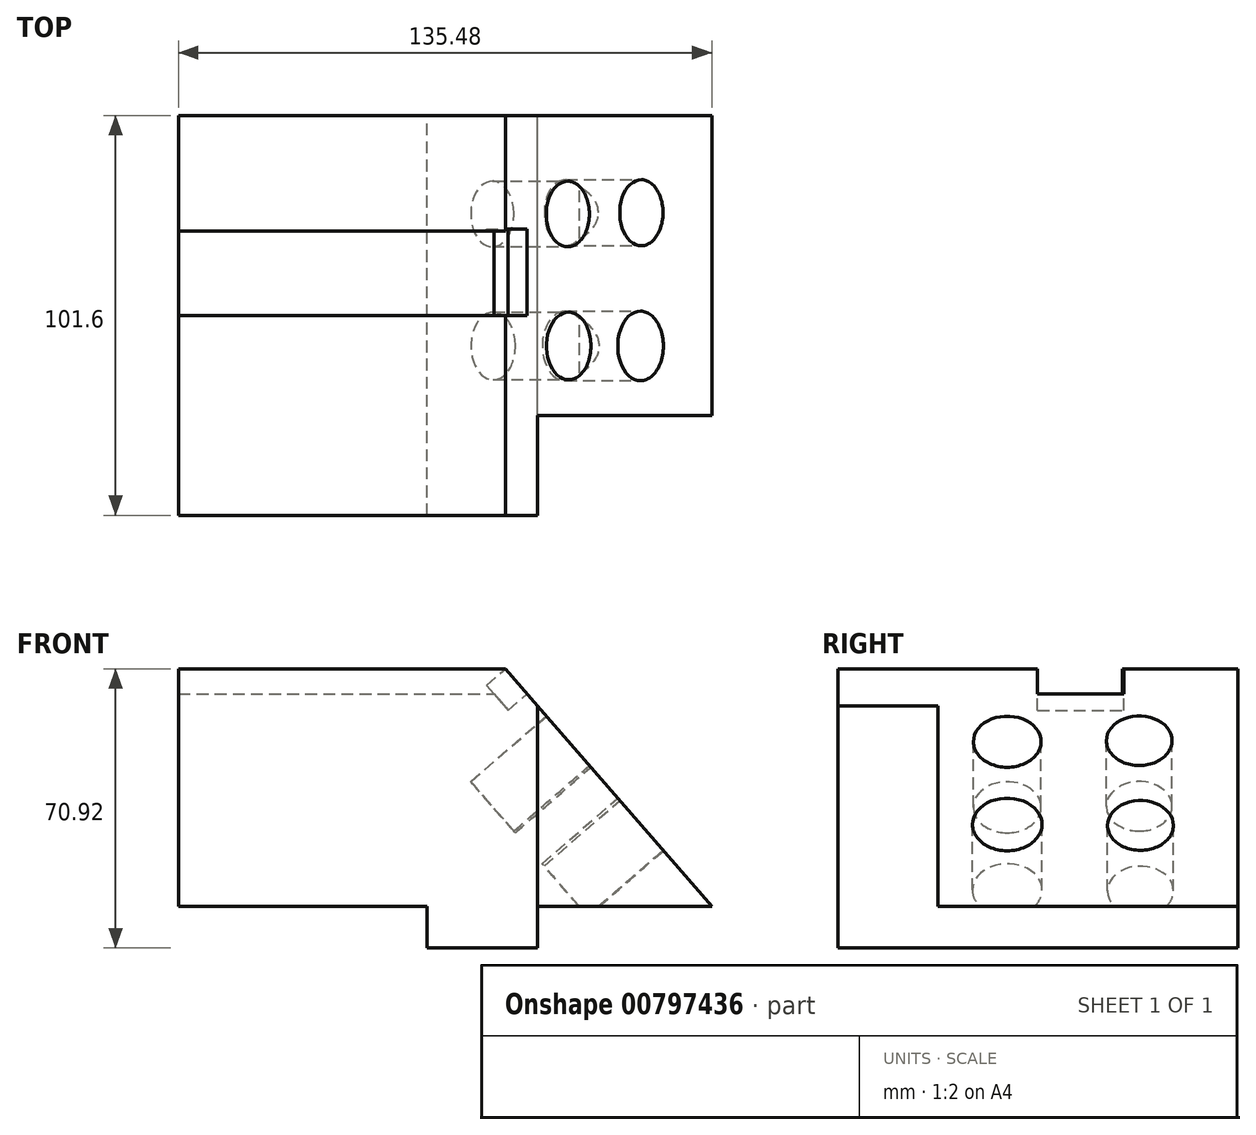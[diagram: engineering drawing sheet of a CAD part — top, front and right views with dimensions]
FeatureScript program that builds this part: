
annotation { "Feature Type Name" : "Feature", "Feature Type Description" : "" }
export const myFeature = defineFeature(function(context is Context, id is Id, definition is map)
    precondition{}
    {
        {
            var Q0;
            Q0=qCreatedBy(makeId("Front.planeOp"),FACE);
            var sketch = newSketch(context, id + "F0", { "sketchPlane" : qUnion([Q0])});
            skLineSegment(sketch, "E0.bottom", {"start": v(-53.31, 36.98) * mm, "end": v(29.7, 36.98) * mm});
            skLineSegment(sketch, "E0.top", {"start": v(-53.31, -23.38) * mm, "end": v(9.77, -23.38) * mm});
            skLineSegment(sketch, "E0.left", {"start": v(-53.31, 36.98) * mm, "end": v(-53.31, -23.38) * mm});
            skLineSegment(sketch, "E1", {"start": v(82.17, -23.38) * mm, "end": v(29.7, 36.98) * mm});
            skLineSegment(sketch, "E2", {"start": v(37.88, -23.38) * mm, "end": v(82.17, -23.38) * mm});
            skLineSegment(sketch, "E3.top", {"start": v(9.77, -33.94) * mm, "end": v(37.88, -33.94) * mm});
            skLineSegment(sketch, "E3.left", {"start": v(9.77, -23.38) * mm, "end": v(9.77, -33.94) * mm});
            skLineSegment(sketch, "E3.right", {"start": v(37.88, -23.38) * mm, "end": v(37.88, -33.94) * mm});
            skPoint(sketch, "E4.orphan", {"position": v(29.7, -23.38) * mm});
            skSolve(sketch);
        }
        {
            var Q0;
            Q0=makeQuery(id+"F0.imprint","IMPRINT",FACE,{"disambiguationData":[TD([[makeQuery(id+"F0.imprint","IMPRINT",EDGE,{"derivedFrom":sQuery(id+"F0.wireOp",EDGE,"E0.bottom")}),-1.0]])]});
            extrude(context, id + "F1", {"entities" : qUnion([Q0]), "depth" : 101.6 * mm, "offsetDistance" : 25.4 * mm});
        }
        {
            var Q0;
            Q0=makeQuery(id+"F1.opExtrude","SWEPT_FACE",FACE,{"disambiguationData":[OSD([sQuery(id+"F0.wireOp",EDGE,"E0.bottom")])]});
            var sketch = newSketch(context, id + "F2", { "sketchPlane" : qUnion([Q0])});
            skLineSegment(sketch, "E5.bottom", {"start": v(-53.31, -50.85) * mm, "end": v(29.7, -50.85) * mm});
            skLineSegment(sketch, "E5.top", {"start": v(-53.31, -29.33) * mm, "end": v(29.7, -29.33) * mm});
            skLineSegment(sketch, "E5.left", {"start": v(-53.31, -50.85) * mm, "end": v(-53.31, -29.33) * mm});
            skLineSegment(sketch, "E5.right", {"start": v(29.7, -50.85) * mm, "end": v(29.7, -29.33) * mm});
            skSolve(sketch);
        }
        {
            var Q0;
            Q0=makeQuery(id+"F2.imprint","IMPRINT",FACE,{"disambiguationData":[TD([[makeQuery(id+"F2.imprint","IMPRINT",EDGE,{"derivedFrom":sQuery(id+"F2.wireOp",EDGE,"E5.bottom")}),1.0]])]});
            extrude(context, id + "F3", {"entities" : qUnion([Q0]), "operationType" : NewBodyOperationType.REMOVE, "oppositeDirection" : true, "depth" : 6.35 * mm, "offsetDistance" : 25.4 * mm});
        }
        {
            var Q0;
            Q0=makeQuery(id+"F1.opExtrude","SWEPT_FACE",FACE,{"disambiguationData":[OSD([sQuery(id+"F0.wireOp",EDGE,"E1")])]});
            var sketch = newSketch(context, id + "F4", { "sketchPlane" : qUnion([Q0])});
            skLineSegment(sketch, "E6.bottom", {"start": v(-50.85, 8.43) * mm, "end": v(-28.85, 8.43) * mm});
            skLineSegment(sketch, "E6.top", {"start": v(-50.85, 0) * mm, "end": v(-28.85, 0) * mm});
            skLineSegment(sketch, "E6.left", {"start": v(-50.85, 8.43) * mm, "end": v(-50.85, 0) * mm});
            skLineSegment(sketch, "E6.right", {"start": v(-28.85, 8.43) * mm, "end": v(-28.85, 0) * mm});
            skCircle(sketch, "E7", {"center": v(-58.55, -16.1) * mm, "radius": 8.6 * mm});
            skCircle(sketch, "E8", {"center": v(-58.55, -43.95) * mm, "radius": 8.84 * mm});
            skCircle(sketch, "E9", {"center": v(-25.01, -15.78) * mm, "radius": 8.33 * mm});
            skCircle(sketch, "E10", {"center": v(-24.7, -44.27) * mm, "radius": 8.37 * mm});
            skSolve(sketch);
        }
        {
            var Q0;
            Q0=makeQuery(id+"F4.imprint","IMPRINT",FACE,{"disambiguationData":[TD([[makeQuery(id+"F4.imprint","IMPRINT",EDGE,{"derivedFrom":sQuery(id+"F4.wireOp",EDGE,"E6.top")}),1.0]])]});
            extrude(context, id + "F5", {"entities" : qUnion([Q0]), "operationType" : NewBodyOperationType.REMOVE, "oppositeDirection" : true, "depth" : 6.35 * mm, "offsetDistance" : 25.4 * mm});
        }
        {
            var Q0;
            Q0=makeQuery(id+"F4.imprint","IMPRINT",FACE,{"disambiguationData":[TD([[makeQuery(id+"F4.imprint","IMPRINT",EDGE,{"derivedFrom":sQuery(id+"F4.wireOp",EDGE,"E7")}),1.0]])]});
            var Q1;
            Q1=makeQuery(id+"F4.imprint","IMPRINT",FACE,{"disambiguationData":[TD([[makeQuery(id+"F4.imprint","IMPRINT",EDGE,{"derivedFrom":sQuery(id+"F4.wireOp",EDGE,"E9")}),1.0]])]});
            var Q2;
            Q2=makeQuery(id+"F4.imprint","IMPRINT",FACE,{"disambiguationData":[TD([[makeQuery(id+"F4.imprint","IMPRINT",EDGE,{"derivedFrom":sQuery(id+"F4.wireOp",EDGE,"E10")}),1.0]])]});
            var Q3;
            Q3=makeQuery(id+"F4.imprint","IMPRINT",FACE,{"disambiguationData":[TD([[makeQuery(id+"F4.imprint","IMPRINT",EDGE,{"derivedFrom":sQuery(id+"F4.wireOp",EDGE,"E8")}),1.0]])]});
            extrude(context, id + "F6", {"entities" : qUnion([Q0, Q1, Q2, Q3]), "operationType" : NewBodyOperationType.REMOVE, "oppositeDirection" : true, "depth" : 25.4 * mm, "offsetDistance" : 25.4 * mm});
        }
        {
            var Q0;
            Q0=makeQuery(id+"F1.opExtrude","CAP_FACE",FACE,{"disambiguationData":[OSD([sQuery(id+"F0.wireOp",EDGE,"E0.bottom"),sQuery(id+"F0.wireOp",EDGE,"E0.top"),sQuery(id+"F0.wireOp",EDGE,"E0.left"),sQuery(id+"F0.wireOp",EDGE,"E1"),sQuery(id+"F0.wireOp",EDGE,"E2"),sQuery(id+"F0.wireOp",EDGE,"E3.top"),sQuery(id+"F0.wireOp",EDGE,"E3.left"),sQuery(id+"F0.wireOp",EDGE,"E3.right")])],"isStart":false});
            var sketch = newSketch(context, id + "F7", { "sketchPlane" : qUnion([Q0])});
            skLineSegment(sketch, "E11", {"start": v(37.88, -23.38) * mm, "end": v(37.88, 27.58) * mm});
            skLineSegment(sketch, "E12", {"start": v(37.88, 27.58) * mm, "end": v(82.17, -23.38) * mm});
            skLineSegment(sketch, "E13", {"start": v(82.17, -23.38) * mm, "end": v(37.88, -23.38) * mm});
            skSolve(sketch);
        }
        {
            var Q0;
            Q0=makeQuery(id+"F7.imprint","IMPRINT",FACE,{"disambiguationData":[TD([[makeQuery(id+"F7.imprint","IMPRINT",EDGE,{"derivedFrom":sQuery(id+"F7.wireOp",EDGE,"E11")}),-1.0]])]});
            extrude(context, id + "F8", {"entities" : qUnion([Q0]), "operationType" : NewBodyOperationType.REMOVE, "oppositeDirection" : true, "depth" : 25.4 * mm, "offsetDistance" : 25.4 * mm});
        }
    });
